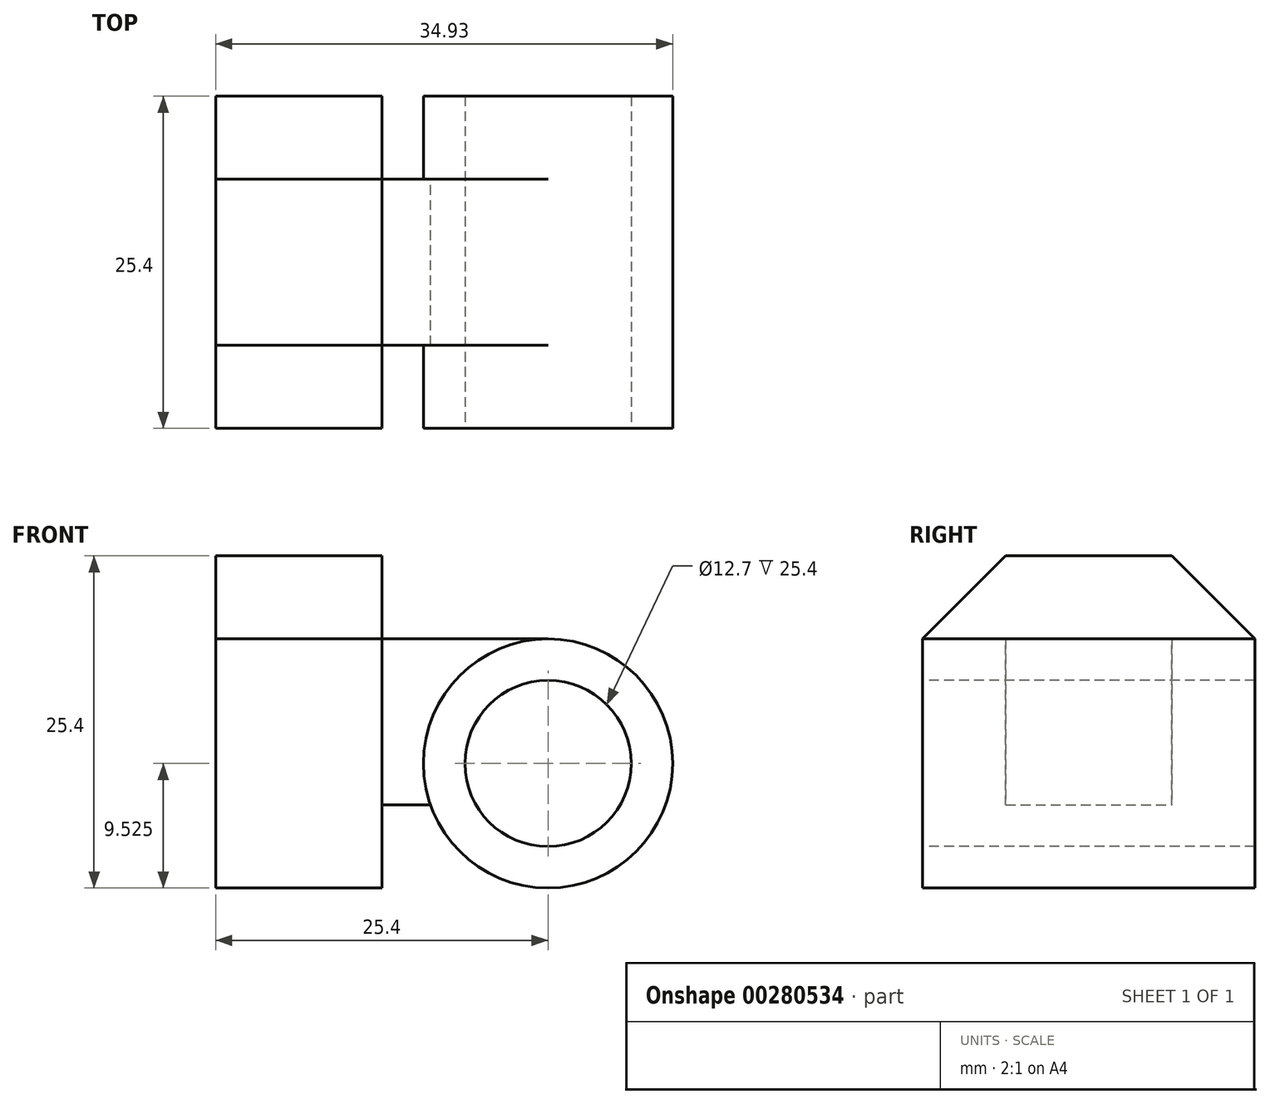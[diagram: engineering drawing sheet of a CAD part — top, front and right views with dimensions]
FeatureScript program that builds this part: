
annotation { "Feature Type Name" : "Feature", "Feature Type Description" : "" }
export const myFeature = defineFeature(function(context is Context, id is Id, definition is map)
    precondition{}
    {
        {
            var Q0;
            Q0=qCreatedBy(makeId("Right.planeOp"),FACE);
            var sketch = newSketch(context, id + "F0", { "sketchPlane" : qUnion([Q0])});
            skLineSegment(sketch, "E0", {"start": v(0, 0) * mm, "end": v(-12.7, 0) * mm});
            skLineSegment(sketch, "E1", {"start": v(-12.7, 0) * mm, "end": v(-12.7, 19.05) * mm});
            skLineSegment(sketch, "E2", {"start": v(-12.7, 19.05) * mm, "end": v(-6.35, 25.4) * mm});
            skLineSegment(sketch, "E3", {"start": v(-6.35, 25.4) * mm, "end": v(6.35, 25.4) * mm});
            skLineSegment(sketch, "E4", {"start": v(6.35, 25.4) * mm, "end": v(12.7, 19.05) * mm});
            skLineSegment(sketch, "E5", {"start": v(12.7, 19.05) * mm, "end": v(12.7, 0) * mm});
            skLineSegment(sketch, "E6", {"start": v(12.7, 0) * mm, "end": v(0, 0) * mm});
            skSolve(sketch);
        }
        {
            var Q0;
            Q0 = qSketchRegion(id + "F0", true);
            extrude(context, id + "F1", {"entities" : qUnion([Q0]), "depth" : 12.7 * mm});
        }
        {
            var Q0;
            Q0=makeQuery(id+"F1.opExtrude","CAP_FACE",FACE,{"disambiguationData":[OSD([sQuery(id+"F0.wireOp",EDGE,"E0"),sQuery(id+"F0.wireOp",EDGE,"E1"),sQuery(id+"F0.wireOp",EDGE,"E2"),sQuery(id+"F0.wireOp",EDGE,"E3"),sQuery(id+"F0.wireOp",EDGE,"E4"),sQuery(id+"F0.wireOp",EDGE,"E5"),sQuery(id+"F0.wireOp",EDGE,"E6")])],"isStart":false});
            var sketch = newSketch(context, id + "F2", { "sketchPlane" : qUnion([Q0])});
            skLineSegment(sketch, "E7.bottom", {"start": v(-6.35, 6.35) * mm, "end": v(6.35, 6.35) * mm});
            skLineSegment(sketch, "E7.top", {"start": v(-6.35, 19.05) * mm, "end": v(6.35, 19.05) * mm});
            skLineSegment(sketch, "E7.left", {"start": v(-6.35, 6.35) * mm, "end": v(-6.35, 19.05) * mm});
            skLineSegment(sketch, "E7.right", {"start": v(6.35, 6.35) * mm, "end": v(6.35, 19.05) * mm});
            skSolve(sketch);
        }
        {
            var Q0;
            Q0 = qSketchRegion(id + "F2", true);
            extrude(context, id + "F3", {"entities" : qUnion([Q0]), "operationType" : NewBodyOperationType.ADD, "depth" : 12.7 * mm});
        }
        {
            var Q0;
            Q0=qCreatedBy(makeId("Front.planeOp"),FACE);
            var sketch = newSketch(context, id + "F4", { "sketchPlane" : qUnion([Q0])});
            skCircle(sketch, "E8", {"center": v(25.4, 9.53) * mm, "radius": 9.53 * mm});
            skSolve(sketch);
        }
        {
            var Q0;
            Q0 = qSketchRegion(id + "F4", true);
            extrude(context, id + "F5", {"entities" : qUnion([Q0]), "operationType" : NewBodyOperationType.ADD, "endBound" : BoundingType.SYMMETRIC, "depth" : 25.4 * mm});
        }
        {
            var Q0;
            Q0=makeQuery(id+"F5.opExtrude","CAP_FACE",FACE,{"disambiguationData":[OSD([sQuery(id+"F4.wireOp",EDGE,"E8")])],"isStart":false});
            var sketch = newSketch(context, id + "F6", { "sketchPlane" : qUnion([Q0])});
            skCircle(sketch, "E9", {"center": v(25.4, 9.53) * mm, "radius": 6.35 * mm});
            skSolve(sketch);
        }
        {
            var Q0;
            Q0=makeQuery(id+"F6.imprint","IMPRINT",FACE,{"disambiguationData":[TD([[makeQuery(id+"F6.imprint","IMPRINT",EDGE,{"derivedFrom":sQuery(id+"F6.wireOp",EDGE,"E9")}),1.0]])]});
            extrude(context, id + "F7", {"entities" : qUnion([Q0]), "operationType" : NewBodyOperationType.REMOVE, "oppositeDirection" : true, "depth" : 50.8 * mm});
        }
    });
